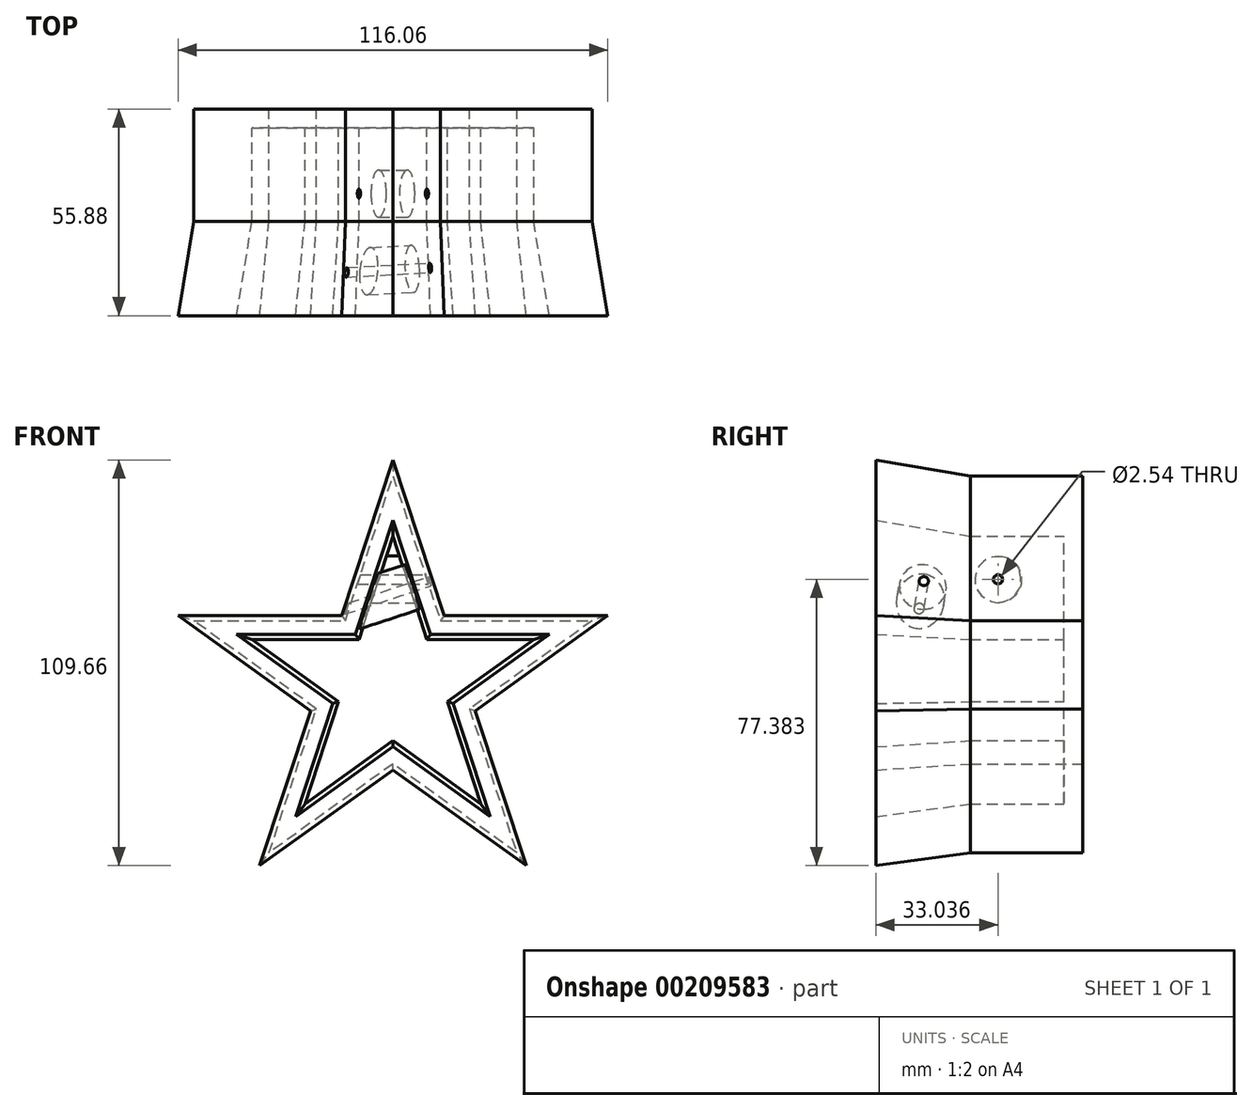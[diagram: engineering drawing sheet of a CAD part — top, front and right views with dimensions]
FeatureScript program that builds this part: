
annotation { "Feature Type Name" : "Feature", "Feature Type Description" : "" }
export const myFeature = defineFeature(function(context is Context, id is Id, definition is map)
    precondition{}
    {
        {
            var Q0;
            Q0=qCreatedBy(makeId("Front.planeOp"),FACE);
            var sketch = newSketch(context, id + "F0", { "sketchPlane" : qUnion([Q0])});
            skLineSegment(sketch, "E0", {"start": v(-47.56, 0) * mm, "end": v(-23.78, 72.4) * mm});
            skLineSegment(sketch, "E1", {"start": v(-23.78, 72.4) * mm, "end": v(0, 0) * mm});
            skLineSegment(sketch, "E2", {"start": v(0, 0) * mm, "end": v(-61.88, 44.47) * mm});
            skLineSegment(sketch, "E3", {"start": v(-61.88, 44.47) * mm, "end": v(14.32, 44.47) * mm});
            skLineSegment(sketch, "E4", {"start": v(14.32, 44.47) * mm, "end": v(-47.56, 0) * mm});
            skPoint(sketch, "E5", {"position": v(-23.78, 17.09) * mm});
            skSolve(sketch);
        }
        {
            var Q0;
            Q0 = qSketchRegion(id + "F0", true);
            extrude(context, id + "F1", {"entities" : qUnion([Q0]), "depth" : 25.4 * mm, "hasDraft" : true, "draftAngle" : 3 * degree, "hasSecondDirection" : true, "secondDirectionOppositeDirection" : true, "secondDirectionDepth" : 25.4 * mm});
        }
        {
            var Q0;
            {var subQ0=sQuery(id+"F0.wireOp",EDGE,"E1");Q0=makeQuery(id+"F1.*.split.splitOp","SPLIT",FACE,{"derivedFrom":makeQuery(id+"F1.opExtrude","SWEPT_FACE",FACE,{"disambiguationData":[OSD([subQ0]),TDD([makeQuery(id+"F0.imprint","IMPRINT",EDGE,{"disambiguationData":[TD([[makeQuery(id+"F0.imprint","INTERSECT",VERTEX,{"derivedFrom":[sQuery(id+"F0.wireOp",EDGE,"E0"),subQ0]}),-1.0]])],"derivedFrom":subQ0})])]})});}
            var sketch = newSketch(context, id + "F2", { "sketchPlane" : qUnion([Q0])});
            skCircle(sketch, "E6", {"center": v(-12.72, 61.5) * mm, "radius": 6.35 * mm});
            skPoint(sketch, "E7", {"position": v(0, 61.5) * mm});
            skPoint(sketch, "E8", {"position": v(-12.72, 47.29) * mm});
            skSolve(sketch);
        }
        {
            var Q0;
            Q0=makeQuery(id+"F2.imprint","IMPRINT",FACE,{"disambiguationData":[TD([[makeQuery(id+"F2.imprint","IMPRINT",EDGE,{"derivedFrom":sQuery(id+"F2.wireOp",EDGE,"E6")}),1.0]])]});
            var Q1;
            Q1=sQuery(id+"F2.wireOp",EDGE,"E6");
            var Q2;
            {var subQ0=sQuery(id+"F0.wireOp",EDGE,"E0");Q2=makeQuery(id+"F1.*.split.splitOp","SPLIT",FACE,{"derivedFrom":makeQuery(id+"F1.opExtrude","SWEPT_FACE",FACE,{"disambiguationData":[OSD([subQ0]),TDD([makeQuery(id+"F0.imprint","IMPRINT",EDGE,{"disambiguationData":[TD([[makeQuery(id+"F0.imprint","INTERSECT",VERTEX,{"derivedFrom":[subQ0,sQuery(id+"F0.wireOp",EDGE,"E1")]}),1.0]])],"derivedFrom":subQ0})])]})});}
            extrude(context, id + "F3", {"entities" : qUnion([Q0]), "operationType" : NewBodyOperationType.REMOVE, "surfaceEntities" : qUnion([Q1]), "endBound" : BoundingType.UP_TO_NEXT, "oppositeDirection" : true, "endBoundEntityFace" : qUnion([Q2]), "depth" : 25.4 * mm});
        }
        {
            var Q0;
            Q0=qCreatedBy(makeId("Right.planeOp"),FACE);
            var sketch = newSketch(context, id + "F4", { "sketchPlane" : qUnion([Q0])});
            skCircle(sketch, "E9", {"center": v(7.64, 60.68) * mm, "radius": 6.35 * mm});
            skSolve(sketch);
        }
        {
            var Q0;
            Q0=makeQuery(id+"F4.imprint","IMPRINT",FACE,{"disambiguationData":[TD([[makeQuery(id+"F4.imprint","IMPRINT",EDGE,{"derivedFrom":sQuery(id+"F4.wireOp",EDGE,"E9")}),1.0]])]});
            extrude(context, id + "F5", {"entities" : qUnion([Q0]), "operationType" : NewBodyOperationType.REMOVE, "endBound" : BoundingType.THROUGH_ALL, "oppositeDirection" : true, "depth" : 25.4 * mm});
        }
        {
            var Q0;
            Q0=makeQuery(id+"F1.opExtrude","CAP_FACE",FACE,{"disambiguationData":[OSD([sQuery(id+"F0.wireOp",EDGE,"E0"),sQuery(id+"F0.wireOp",EDGE,"E1"),sQuery(id+"F0.wireOp",EDGE,"E2"),sQuery(id+"F0.wireOp",EDGE,"E3"),sQuery(id+"F0.wireOp",EDGE,"E4")])],"isStart":false});
            shell(context, id + "F6", {"entities" : qUnion([Q0]), "thickness" : 5.08 * mm, "oppositeDirection" : true});
        }
    });
